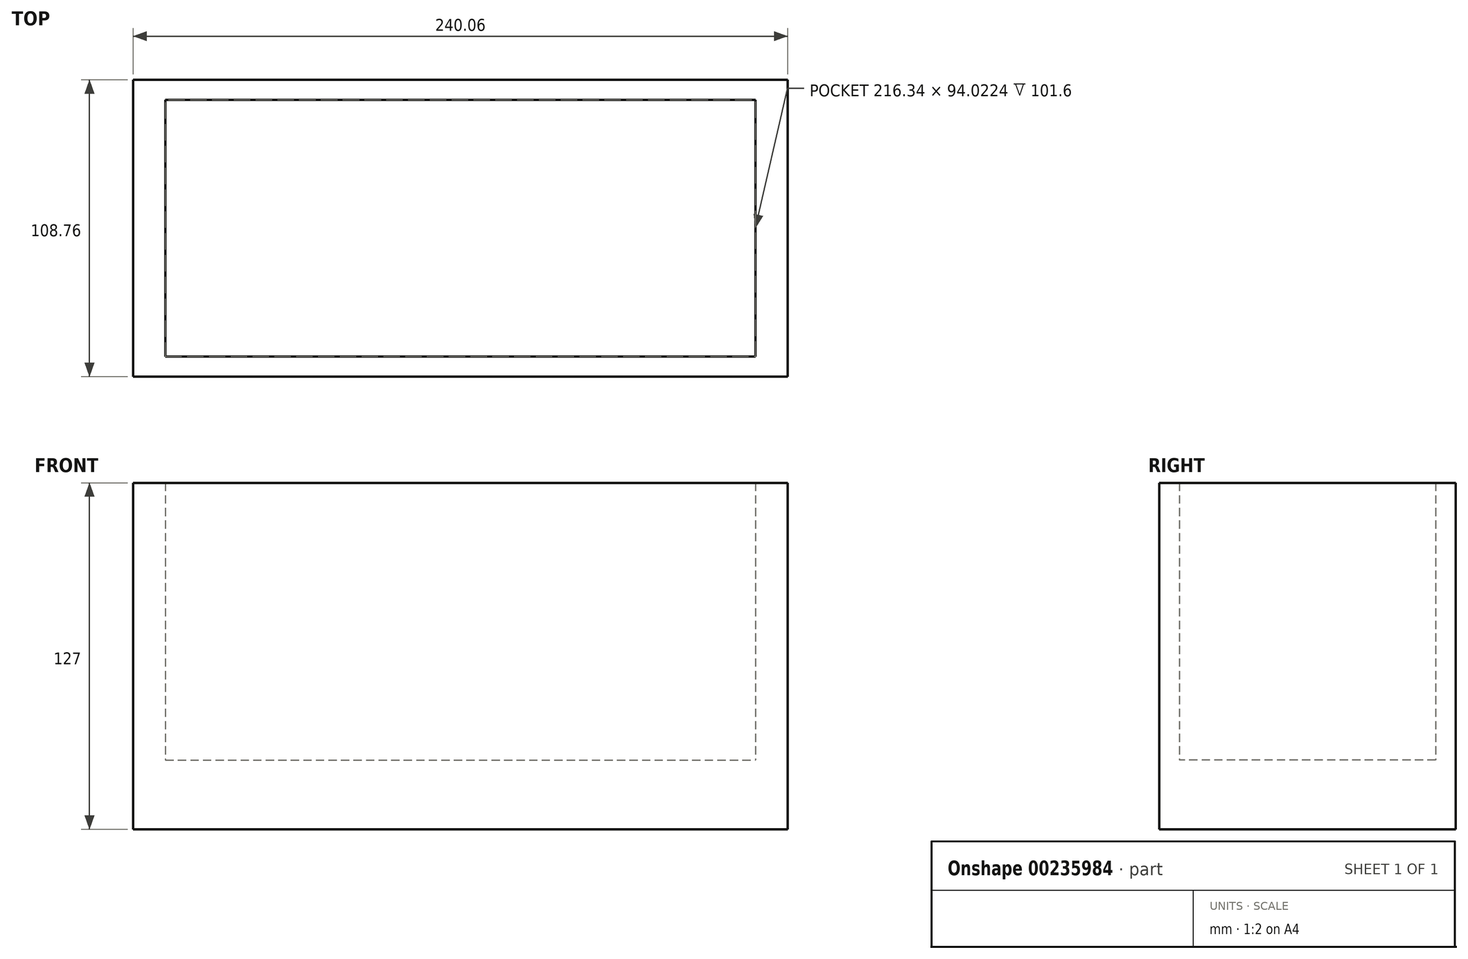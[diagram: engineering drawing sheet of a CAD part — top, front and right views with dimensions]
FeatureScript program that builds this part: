
annotation { "Feature Type Name" : "Feature", "Feature Type Description" : "" }
export const myFeature = defineFeature(function(context is Context, id is Id, definition is map)
    precondition{}
    {
        {
            var Q0;
            Q0=qCreatedBy(makeId("Top.planeOp"),FACE);
            var sketch = newSketch(context, id + "F0", { "sketchPlane" : qUnion([Q0])});
            skLineSegment(sketch, "E0.bottom", {"start": v(-108.17, 47.01) * mm, "end": v(108.17, 47.01) * mm});
            skLineSegment(sketch, "E0.top", {"start": v(-108.17, -47.01) * mm, "end": v(108.17, -47.01) * mm});
            skLineSegment(sketch, "E0.left", {"start": v(-108.17, 47.01) * mm, "end": v(-108.17, -47.01) * mm});
            skLineSegment(sketch, "E0.right", {"start": v(108.17, 47.01) * mm, "end": v(108.17, -47.01) * mm});
            skPoint(sketch, "E0.middle", {"position": v(0, 0) * mm});
            skSolve(sketch);
        }
        {
            var Q0;
            Q0=makeQuery(id+"F0.imprint","IMPRINT",FACE,{"disambiguationData":[TD([[makeQuery(id+"F0.imprint","IMPRINT",EDGE,{"derivedFrom":sQuery(id+"F0.wireOp",EDGE,"E0.bottom")}),-1.0]])]});
            var sketch = newSketch(context, id + "F1", { "sketchPlane" : qUnion([Q0])});
            skLineSegment(sketch, "E1.bottom", {"start": v(-115.6, 51.14) * mm, "end": v(115.6, 51.14) * mm});
            skLineSegment(sketch, "E1.top", {"start": v(-115.6, -51.14) * mm, "end": v(115.6, -51.14) * mm});
            skLineSegment(sketch, "E1.left", {"start": v(-115.6, 51.14) * mm, "end": v(-115.6, -51.14) * mm});
            skLineSegment(sketch, "E1.right", {"start": v(115.6, 51.14) * mm, "end": v(115.6, -51.14) * mm});
            skPoint(sketch, "E1.middle", {"position": v(0, 0) * mm});
            skSolve(sketch);
        }
        {
            var Q0;
            Q0=makeQuery(id+"F0.imprint","IMPRINT",FACE,{"disambiguationData":[TD([[makeQuery(id+"F0.imprint","IMPRINT",EDGE,{"derivedFrom":sQuery(id+"F0.wireOp",EDGE,"E0.bottom")}),-1.0]])]});
            var sketch = newSketch(context, id + "F2", { "sketchPlane" : qUnion([Q0])});
            skLineSegment(sketch, "E2.bottom", {"start": v(-120.03, 54.38) * mm, "end": v(120.03, 54.38) * mm});
            skLineSegment(sketch, "E2.top", {"start": v(-120.03, -54.38) * mm, "end": v(120.03, -54.38) * mm});
            skLineSegment(sketch, "E2.left", {"start": v(-120.03, 54.38) * mm, "end": v(-120.03, -54.38) * mm});
            skLineSegment(sketch, "E2.right", {"start": v(120.03, 54.38) * mm, "end": v(120.03, -54.38) * mm});
            skPoint(sketch, "E2.middle", {"position": v(0, 0) * mm});
            skSolve(sketch);
        }
        {
            var Q0;
            Q0=makeQuery(id+"F0.imprint","IMPRINT",FACE,{"disambiguationData":[TD([[makeQuery(id+"F0.imprint","IMPRINT",EDGE,{"derivedFrom":sQuery(id+"F0.wireOp",EDGE,"E0.bottom")}),-1.0]])]});
            extrude(context, id + "F3", {"entities" : qUnion([Q0]), "depth" : 25.4 * mm});
        }
        {
            var Q0;
            Q0=makeQuery(id+"F1.imprint","IMPRINT",FACE,{"disambiguationData":[TD([[makeQuery(id+"F1.imprint","IMPRINT",EDGE,{"derivedFrom":sQuery(id+"F1.wireOp",EDGE,"E1.bottom")}),-1.0]])]});
            extrude(context, id + "F4", {"entities" : qUnion([Q0]), "operationType" : NewBodyOperationType.ADD, "depth" : 50.8 * mm});
        }
        {
            var Q0;
            Q0=makeQuery(id+"F2.imprint","IMPRINT",FACE,{"disambiguationData":[TD([[makeQuery(id+"F2.imprint","IMPRINT",EDGE,{"derivedFrom":sQuery(id+"F2.wireOp",EDGE,"E2.bottom")}),-1.0]])]});
            extrude(context, id + "F5", {"entities" : qUnion([Q0]), "operationType" : NewBodyOperationType.ADD, "depth" : 127 * mm});
        }
    });
